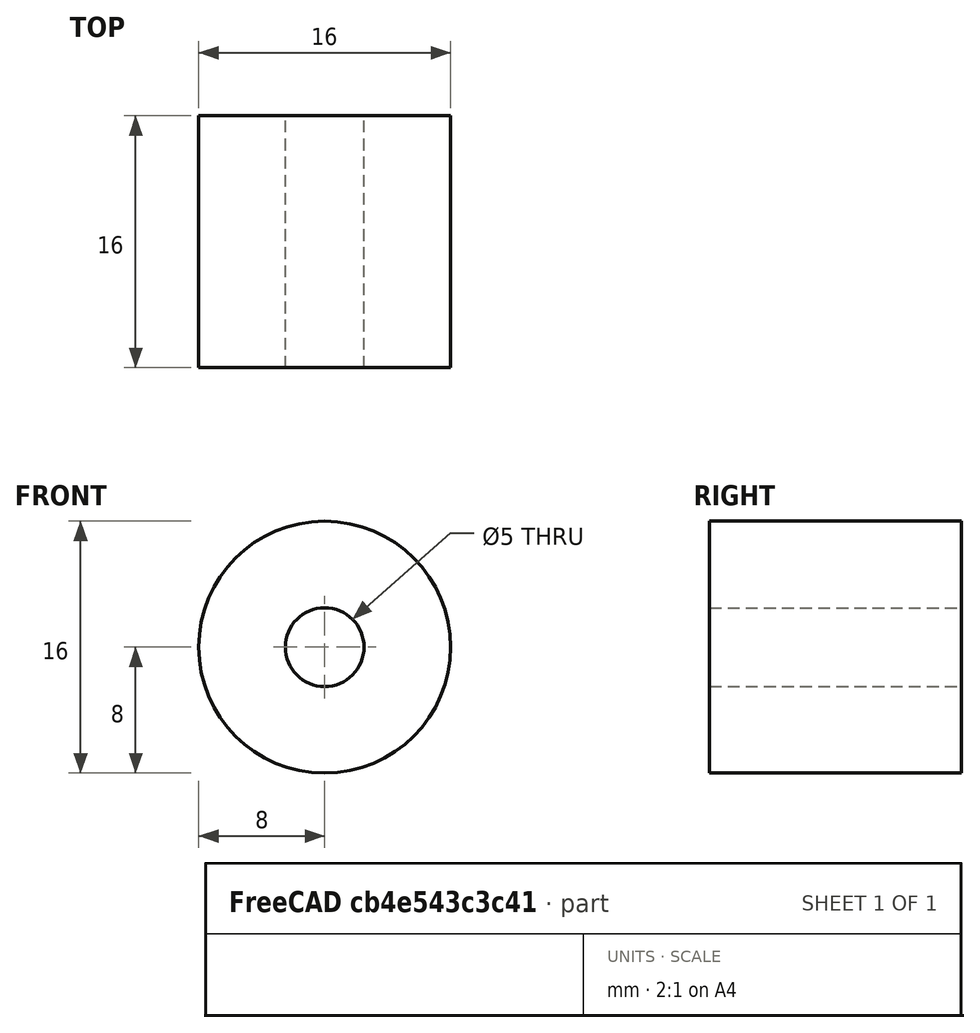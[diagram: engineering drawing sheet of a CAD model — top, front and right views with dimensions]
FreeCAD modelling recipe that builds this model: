
FCSTD DOCUMENT  (FreeCAD 0.19R)
Label: pulley_replacement
License: All rights reserved
LicenseURL: http://en.wikipedia.org/wiki/All_rights_reserved
objects: Sketcher::SketchObject×1, PartDesign::Revolution×1
note: 3 computed .brp shape members not serialized (recipe doc carries the construction recipe); baked Part::Feature solids carry a one-line shape summary decoded from their .brp

FEATURE [Sketcher::SketchObject] Sketch
  MapMode = 5
  sketch-geometry (4):
    g0: LineSegment StartX=2.5 StartY=0 StartZ=0 EndX=2.5 EndY=16 EndZ=0
    g1: LineSegment StartX=2.5 StartY=16 StartZ=0 EndX=8 EndY=16 EndZ=0
    g2: LineSegment StartX=8 StartY=0 StartZ=0 EndX=2.5 EndY=0 EndZ=0
    g3: LineSegment StartX=8 StartY=16 StartZ=0 EndX=8 EndY=0 EndZ=0
  constraints (12):
    c: Vertical(g0)
    c: Coincident(g0,g1)
    c: Horizontal(g1)
    c: Coincident(g2,g0)
    c: Horizontal(g2)
    c: DistanceY(g0,g0) = 16
    c: PointOnObject(g0,g-1)
    c: DistanceX(g-1,g2) = 8
    c: DistanceX(g-1,g0) = 2.5
    c: Coincident(g3,g1)
    c: Coincident(g3,g2)
    c: Vertical(g3)
FEATURE [PartDesign::Revolution] Revolution
  AllowMultiFace = false
  Angle = 360
  Axis = (0,1,0)
  Base = (0,0,0)
  Profile = -> Sketch
  ReferenceAxis = -> Sketch [V_Axis]
  Reversed = true
